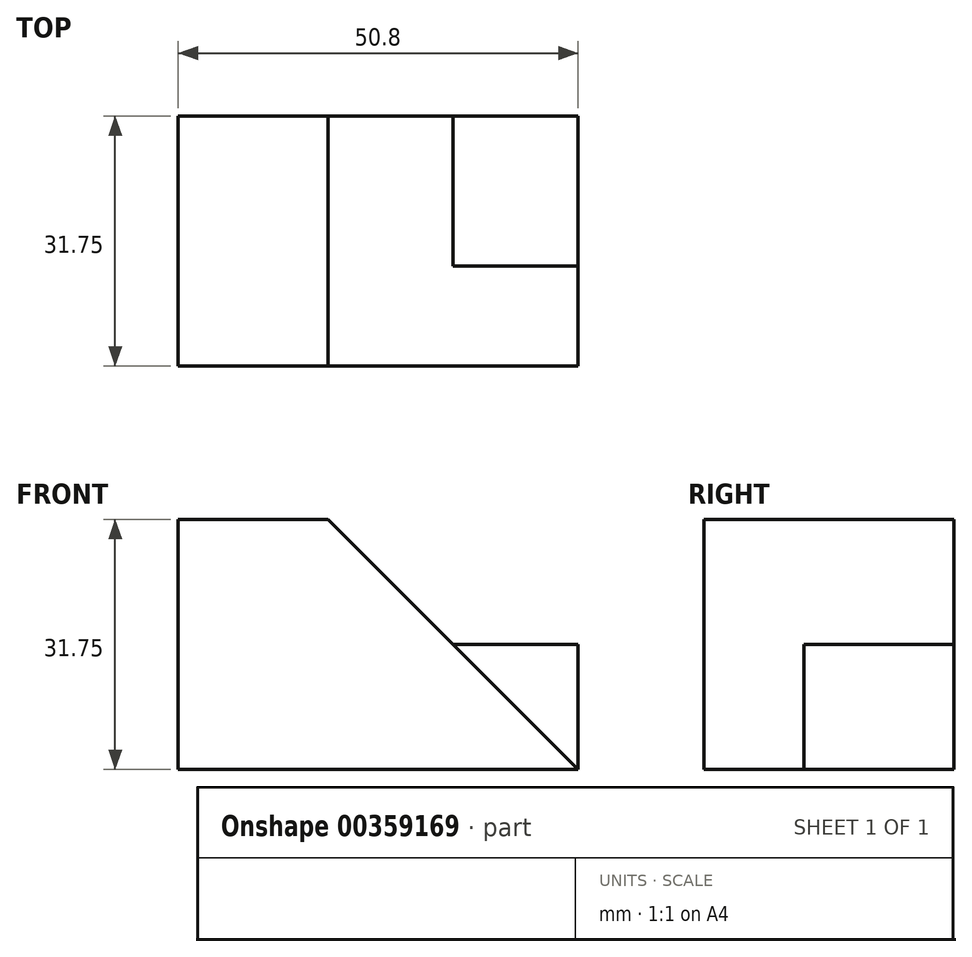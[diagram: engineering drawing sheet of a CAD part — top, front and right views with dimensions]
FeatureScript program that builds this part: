
annotation { "Feature Type Name" : "Feature", "Feature Type Description" : "" }
export const myFeature = defineFeature(function(context is Context, id is Id, definition is map)
    precondition{}
    {
        {
            var Q0;
            Q0=qCreatedBy(makeId("Front.planeOp"),FACE);
            var sketch = newSketch(context, id + "F0", { "sketchPlane" : qUnion([Q0])});
            skLineSegment(sketch, "E0", {"start": v(0, 0) * mm, "end": v(50.8, 0) * mm});
            skLineSegment(sketch, "E1", {"start": v(50.8, 0) * mm, "end": v(50.8, 31.75) * mm});
            skLineSegment(sketch, "E2", {"start": v(50.8, 31.75) * mm, "end": v(0, 31.75) * mm});
            skLineSegment(sketch, "E3", {"start": v(0, 31.75) * mm, "end": v(0, 0) * mm});
            skSolve(sketch);
        }
        {
            var Q0;
            Q0=makeQuery(id+"F0.imprint","IMPRINT",FACE,{"disambiguationData":[TD([[makeQuery(id+"F0.imprint","IMPRINT",EDGE,{"derivedFrom":sQuery(id+"F0.wireOp",EDGE,"E0")}),1.0]])]});
            extrude(context, id + "F1", {"entities" : qUnion([Q0]), "depth" : 31.75 * mm});
        }
        {
            var Q0;
            Q0=makeQuery(id+"F1.opExtrude","CAP_FACE",FACE,{"disambiguationData":[OSD([sQuery(id+"F0.wireOp",EDGE,"E0"),sQuery(id+"F0.wireOp",EDGE,"E1"),sQuery(id+"F0.wireOp",EDGE,"E2"),sQuery(id+"F0.wireOp",EDGE,"E3")])],"isStart":false});
            var sketch = newSketch(context, id + "F2", { "sketchPlane" : qUnion([Q0])});
            skLineSegment(sketch, "E4", {"start": v(50.8, 0) * mm, "end": v(50.8, 31.75) * mm});
            skLineSegment(sketch, "E5", {"start": v(50.8, 31.75) * mm, "end": v(19.05, 31.75) * mm});
            skLineSegment(sketch, "E6", {"start": v(19.05, 31.75) * mm, "end": v(50.8, 0) * mm});
            skSolve(sketch);
        }
        {
            var Q0;
            Q0=makeQuery(id+"F2.imprint","IMPRINT",FACE,{"disambiguationData":[TD([[makeQuery(id+"F2.imprint","IMPRINT",EDGE,{"derivedFrom":sQuery(id+"F2.wireOp",EDGE,"E4")}),1.0]])]});
            extrude(context, id + "F3", {"entities" : qUnion([Q0]), "operationType" : NewBodyOperationType.REMOVE, "oppositeDirection" : true, "depth" : 12.7 * mm});
        }
        {
            var Q0;
            Q0=makeQuery(id+"F3.boolean.opBoolean","COPY",FACE,{"derivedFrom":makeQuery(id+"F3.opExtrude","CAP_FACE",FACE,{"disambiguationData":[OSD([sQuery(id+"F2.wireOp",EDGE,"E4"),sQuery(id+"F2.wireOp",EDGE,"E5"),sQuery(id+"F2.wireOp",EDGE,"E6")])],"isStart":false})});
            var sketch = newSketch(context, id + "F4", { "sketchPlane" : qUnion([Q0])});
            skLineSegment(sketch, "E7", {"start": v(19.05, 31.75) * mm, "end": v(50.8, 31.75) * mm});
            skLineSegment(sketch, "E8", {"start": v(50.8, 31.75) * mm, "end": v(50.8, 15.88) * mm});
            skLineSegment(sketch, "E9", {"start": v(50.8, 15.88) * mm, "end": v(34.92, 15.88) * mm});
            skLineSegment(sketch, "E10", {"start": v(34.92, 15.88) * mm, "end": v(19.05, 31.75) * mm});
            skSolve(sketch);
        }
        {
            var Q0;
            Q0=makeQuery(id+"F4.imprint","IMPRINT",FACE,{"disambiguationData":[TD([[makeQuery(id+"F4.imprint","IMPRINT",EDGE,{"derivedFrom":sQuery(id+"F4.wireOp",EDGE,"E7")}),1.0]])]});
            extrude(context, id + "F5", {"entities" : qUnion([Q0]), "operationType" : NewBodyOperationType.REMOVE, "oppositeDirection" : true, "depth" : 31.75 * mm});
        }
    });
